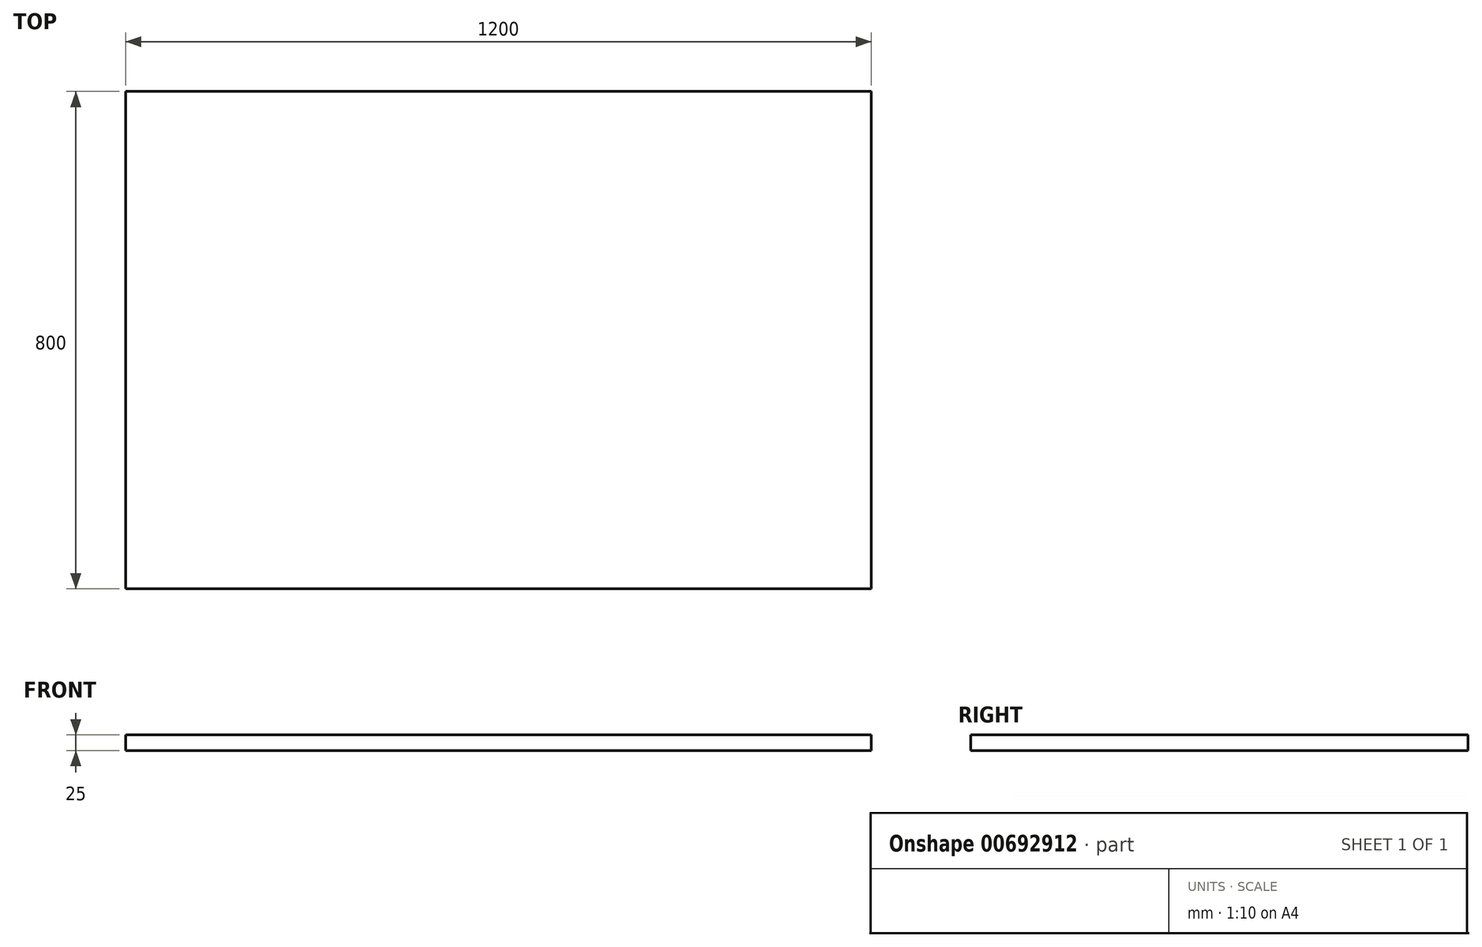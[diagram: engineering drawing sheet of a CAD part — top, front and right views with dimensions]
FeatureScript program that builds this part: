
annotation { "Feature Type Name" : "Feature", "Feature Type Description" : "" }
export const myFeature = defineFeature(function(context is Context, id is Id, definition is map)
    precondition{}
    {
        {
            var Q0;
            Q0=qCreatedBy(makeId("Top.planeOp"),FACE);
            var sketch = newSketch(context, id + "F0", { "sketchPlane" : qUnion([Q0])});
            skLineSegment(sketch, "E0.bottom", {"start": v(0, 0) * mm, "end": v(-1200, 0) * mm});
            skLineSegment(sketch, "E0.top", {"start": v(0, 800) * mm, "end": v(-1200, 800) * mm});
            skLineSegment(sketch, "E0.left", {"start": v(0, 0) * mm, "end": v(0, 800) * mm});
            skLineSegment(sketch, "E0.right", {"start": v(-1200, 0) * mm, "end": v(-1200, 800) * mm});
            skLineSegment(sketch, "E1", {"start": v(-1200, 120) * mm, "end": v(0, 120) * mm, "construction": true});
            skLineSegment(sketch, "E2", {"start": v(-1439.02, 400) * mm, "end": v(341.35, 400) * mm, "construction": true});
            skPoint(sketch, "E2.startSnap0", {"position": v(-1200, 400) * mm});
            skLineSegment(sketch, "E3", {"start": v(-1200, 680) * mm, "end": v(0, 680) * mm, "construction": true});
            skSolve(sketch);
        }
        {
            var Q0;
            Q0 = qSketchRegion(id + "F0", true);
            extrude(context, id + "F1", {"entities" : qUnion([Q0]), "depth" : 25 * mm, "offsetDistance" : 25 * mm});
        }
        {
            var Q0;
            Q0=qCreatedBy(makeId("Top.planeOp"),FACE);
            cPlane(context, id + "F2", {"entities" : qUnion([Q0]), "cplaneType" : CPlaneType.OFFSET, "offset" : 400 * mm, "oppositeDirection" : true, "width" : 150 * mm, "height" : 150 * mm});
        }
        {
            var Q0;
            Q0=qCreatedBy(id+"F2.planeOp",FACE);
            var sketch = newSketch(context, id + "F3", { "sketchPlane" : qUnion([Q0])});
            skLineSegment(sketch, "E4.0.0", {"start": v(0, 800) * mm, "end": v(0, 0) * mm});
            skLineSegment(sketch, "E4.0.1", {"start": v(0, 0) * mm, "end": v(-1200, 0) * mm});
            skLineSegment(sketch, "E4.0.2", {"start": v(-1200, 0) * mm, "end": v(-1200, 800) * mm});
            skLineSegment(sketch, "E4.0.3", {"start": v(-1200, 800) * mm, "end": v(0, 800) * mm});
            skLineSegment(sketch, "E5.0", {"start": v(-1439.02, 400) * mm, "end": v(341.35, 400) * mm, "construction": true});
            skLineSegment(sketch, "E6.0", {"start": v(-1200, 120) * mm, "end": v(0, 120) * mm, "construction": true});
            skLineSegment(sketch, "E7.0", {"start": v(-1200, 680) * mm, "end": v(0, 680) * mm, "construction": true});
            skSolve(sketch);
        }
        {
            var Q0;
            Q0=sQuery(id+"F3.wireOp",EDGE,"E4.0.2");
            var Q1;
            Q1=sQuery(id+"F3.wireOp",EDGE,"E4.0.3");
            var Q2;
            Q2=sQuery(id+"F3.wireOp",EDGE,"E4.0.0");
            var Q3;
            Q3=sQuery(id+"F3.wireOp",EDGE,"E4.0.1");
            extrude(context, id + "F4", {"bodyType" : ToolBodyType.SURFACE, "surfaceEntities" : qUnion([Q0, Q1, Q2, Q3]), "oppositeDirection" : true, "depth" : 10 * mm, "offsetDistance" : 25 * mm});
        }
    });
